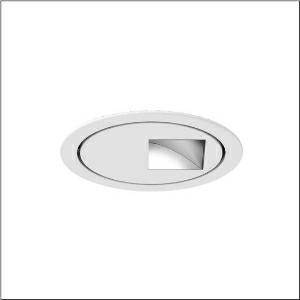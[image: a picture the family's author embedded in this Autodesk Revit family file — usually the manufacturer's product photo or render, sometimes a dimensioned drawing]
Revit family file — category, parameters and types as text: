
# Revit family: lunis_11_mini_round_51dk11b72wm21
name_source: partatom
category: Lighting Fixtures
units: mm (PartAtom-declared; Revit-internal decimal feet)

## family parameters
Cut with Voids When Loaded = No
Host = Face
Light Source = No
Part Type = Normal
Room Calculation Point = No
Round Connector Dimension = Use Diameter
Shared = No

## types (1)
- Lunis 11 mini round (1 x LED 3000K / CRI = 90 (unbekannt), 1930 lm, 3000K)
    Apparent Load = 28 VA
    CIE Flux Codes = 44 77 97 100 100
    Color Rendering = 90
    Color Temperature = 3000K
    Default Elevation = 1800 mm
    Description = Lunis 11 mini round, downlight, light control with wallwasher, of highly reflective aluminium, highly specular, light emission: direct distribution, LED rated luminous flux: 1.930lm, light colour: 930, control gear: ECG, with terminal, 3-pole, mains connection: 220..230V, AC/DC, 0/50..60Hz, LED module, luminaire module, of aluminium, highly specular, white, diameter: 176mm, clamping range: 1..40mm, recessing ring, of plastic, traffic white (RAL 9016), protection rating (complete): IP20, insulation class (complete): insulation class II (safety insulation), certification: CE, permissible ambient temperature for indoor applications: 0..+35°C, packaging unit: 1 piece
    Height = 0 mm  [stored 0 ft]
    Lamp = 1 x LED 3000K / CRI >= 90 (unbekannt)
    Lamp Light Flux = 1930 lm
    Lamp count = 1
    Length = 176 mm
    Luminous efficacy = 69 lm/W
    Manufacturer = Siteco
    ModVariant = No
    Model = 51DK11B72WM21
    Mounting Place = Ceiling
    Mounting Type = Recessed
    Number of Poles = 1
    OnlyDefault = Yes
    Power Factor = 1
    Product Name = Lunis 11 mini round
    Product group = downlight | ceiling recessed
    ProductGroupID = 402
    Protection Class = Protection class II
    Protection Degree = IP 20
    RLX_Detail_Level = 1
    RlxData = <blob elided: 59321 chars, md5=b5ac5997>
    Socket = socket
    Standby Power = 0 W
    System Light Flux = 1930 lm
    System Power = 28 W
    Type Comments = Product without accessories
    Type Image = l_1004772.jpg
    URL = http://relux.com
    VarID = ---
    Voltage = 0 V
    Weight = 0.00 kg
    Width = 176 mm

note: [stored X ft] marks values corroborated as IEEE doubles in the binary element streams (Revit-internal decimal feet)

## geometry (parser evidence)
native form markers: Blend x4, Sweep x12
no freeform markers — native parametric forms only
